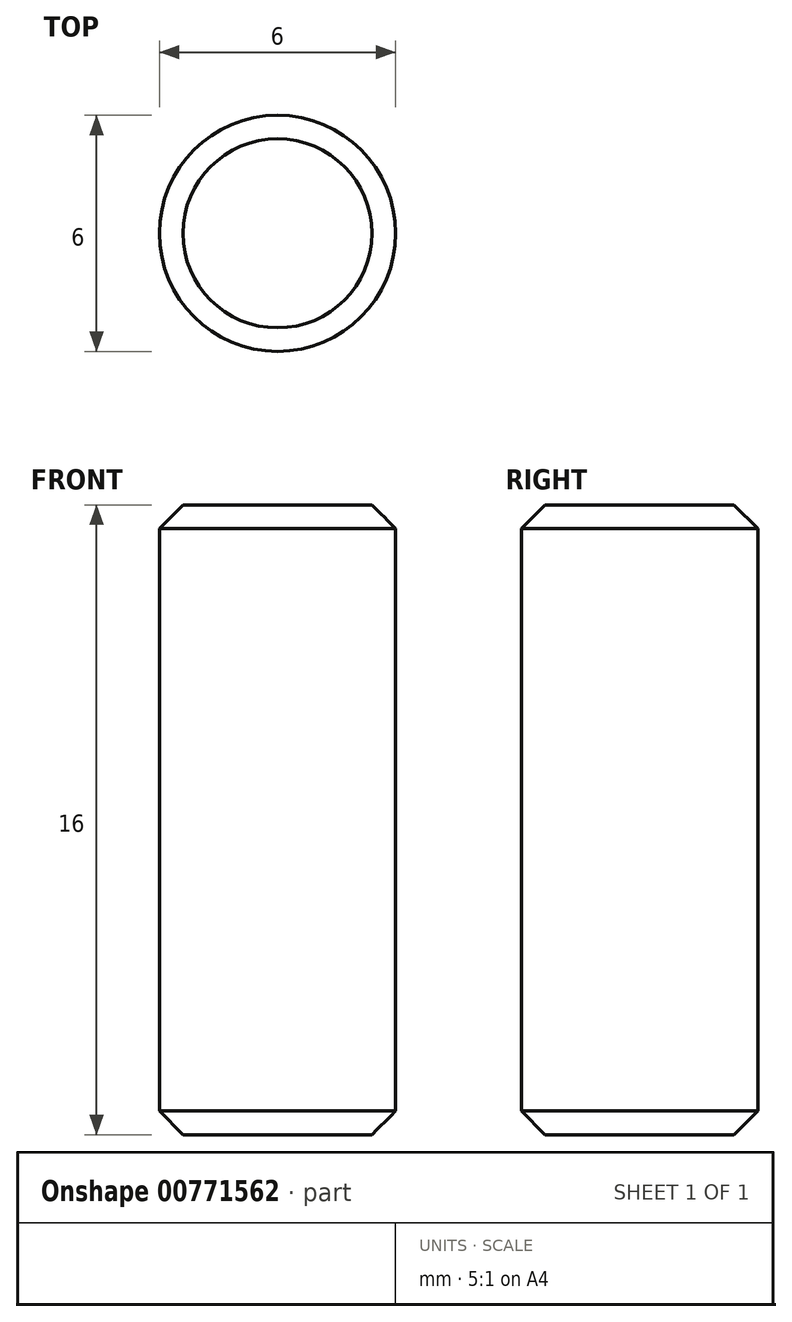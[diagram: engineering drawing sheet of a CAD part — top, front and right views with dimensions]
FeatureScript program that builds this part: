
annotation { "Feature Type Name" : "Feature", "Feature Type Description" : "" }
export const myFeature = defineFeature(function(context is Context, id is Id, definition is map)
    precondition{}
    {
        {
            var Q0;
            Q0=qCreatedBy(makeId("Top.planeOp"),FACE);
            var sketch = newSketch(context, id + "F0", { "sketchPlane" : qUnion([Q0])});
            skCircle(sketch, "E0", {"center": v(0, 0) * mm, "radius": 3 * mm});
            skSolve(sketch);
        }
        {
            var Q0;
            Q0 = qSketchRegion(id + "F0", true);
            extrude(context, id + "F1", {"entities" : qUnion([Q0]), "endBound" : BoundingType.SYMMETRIC, "depth" : 16 * mm, "offsetDistance" : 25 * mm});
        }
        {
            var Q0;
            Q0=makeQuery(id+"F1.opExtrude","CAP_EDGE",EDGE,{"disambiguationData":[OSD([sQuery(id+"F0.wireOp",EDGE,"E0")])],"isStart":false});
            var Q1;
            Q1=makeQuery(id+"F1.opExtrude","CAP_EDGE",EDGE,{"disambiguationData":[OSD([sQuery(id+"F0.wireOp",EDGE,"E0")])],"isStart":true});
            chamfer(context, id + "F2", {"entities" : qUnion([Q0, Q1]), "width" : 0.6 * mm, "tangentPropagation" : true});
        }
    });
